# Revit family: Table-Allermuir-Conic
name_source: partatom
category: Furniture
revit_build: Autodesk Revit Architecture 2012 (Build: 20110309_2315(x64)
units: mm (PartAtom-declared; Revit-internal decimal feet)

## types (5) — shared parameters
04 CSI = 12 51 00
95 CSI = 12510
Assembly Code = E2020200
CAD Blocks URL = http://www.allermuir.net
Color Availability = See price list for material options
Fabric Spec Sheets = http://www.allermuir.net
Glide Finish = Plastic - Allermuir - Black
Leg Support Finish = Metal - Allermuir - Chrome - Polished
Manufacturer = Allermuir
Manufacturer Fax = (419) 887 5805
Pricing URL = http://www.allermuir.net
Product Line = Conic Tables
Product Page URL = http://www.allermuir.net
Specifications URL = http://www.allermuir.net
Stacks = Yes
Subcategory = Tables
Table Top = Laminate - Allermuir - White
URL = http://www.allermuir.net
ecoScorecard Product Page = http://products.ecoscorecard.com

## per-type parameters (varying)
| type | A636 55SS Table Top | A636 6RD Table Top | A638-88SS | A639 107S Table Top | Angle | Diameter | Leg Base  Depth | Leg Base 1 | Leg Base 2 | Leg Base 3 | Leg Base Height | Leg Base Width | Model | Overall Depth | Overall Height | Overall Width | Plugin Data URL | Table Top_Radius | ecoScorecard_data |
| A636 6RD-Conic Tables | No | Yes | No | No | 6.00° | 0' - 11 95/128" | 1' - 10 9/64" | Yes | No | No | 1' - 2 115/128" | 1' - 10 9/64" | A636/6RD | 1' - 11 31/64" | 1' - 4" | 1' - 11 31/64" | http://products.ecoscorecard.com 6RD | 0' - 10" | http://thesenatorgroup.ecoscorecard.com 6RD |
| A636 55SS-Conic Tables | Yes | No | No | No | 6.00° | 1' - 8" | 1' - 10 9/64" | No | No | Yes | 1' - 2 115/128" | 1' - 10 9/64" | A636/55SS | 1' - 9 15/256" | 1' - 4" | 1' - 9 15/256" | http://products.ecoscorecard.com 55SS | 0' - 10" | http://thesenatorgroup.ecoscorecard.com 55SS |
| A638 9RD-Conic Tables | No | Yes | No | No | 15.00° | 1' - 5 197/256" | 2' - 9 197/256" | Yes | No | No | 0' - 10 115/128" | 2' - 9 197/256" | A638/9RD | 2' - 11 69/128" | 1' - 0" | 2' - 11 69/128" | http://products.ecoscorecard.com 9RD | 1' - 4" | http://thesenatorgroup.ecoscorecard.com 9RD |
| A639 107S-Conic Tables | No | No | No | Yes | 15.00° | 1' - 5 197/256" | 2' - 9 197/256" | No | Yes | No | 0' - 10 115/128" | 2' - 9 197/256" | A639-107S | 2' - 2 239/256" | 1' - 0" | 3' - 4 117/128" | http://products.ecoscorecard.com 107S | 1' - 4" | http://thesenatorgroup.ecoscorecard.com 107S |
| A638-88SS-Conic Tables | No | No | Yes | No | 6.00° | 1' - 8" | 2' - 7 53/128" | Yes | No | No | 0' - 10 15/16" | 2' - 7 31/64" | A638-88SS | 2' - 7 53/128" | 1' - 0 5/128" | 1' - 9 15/256" | http://products.ecoscorecard.com | 0' - 10" | http://thesenatorgroup.ecoscorecard.com |

## geometry (parser evidence)
native form markers: Blend x6, Sweep x11
no freeform markers — native parametric forms only
